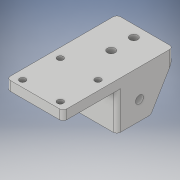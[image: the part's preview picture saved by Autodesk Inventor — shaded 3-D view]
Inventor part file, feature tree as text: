
AUTODESK INVENTOR PART (.ipt)
format: ipt  version: 2018 (Build 220112000, 112)  size: 181,248 bytes
history: native  units: in
note: dims shown in document units (in); Inventor stores cm internally (conversion verified against a paired STEP export)
features: extrude x6, sketch x6, mirror x1, fillet x1
ambient origin geometry x8: Origin, YZ Plane, XZ Plane, XY Plane, X Axis, Y Axis, Z Axis, Center Point
bodies: Solid1 (feature_tree)
feature tree (14):
  extrude  "Extrusion1"  Depth=2.3031in
  extrude  "Extrusion2"  Depth=0.1969in
  extrude  "Extrusion3"  Depth=0.7874in
  extrude  "Extrusion4"  Depth=0.1969in TaperAngle=0.0deg
  extrude  "Extrusion5"  Depth=0.9843in
  mirror  "Mirror1"
  extrude  "Extrusion6"  Depth=0.0787in
  fillet  "Fillet1"  Radius=0.4724in
  sketch  "Sketch1"  dims[d0=1.1811in d1=2.3031in]
  sketch  "Sketch2"  dims[d2=0.1969in d3=0.0in d4=0.126in]
  sketch  "Sketch3"  dims[d5=0.7874in d6=0.7874in]
  sketch  "Sketch4"  dims[d7=0.1378in d8=0.1969in d9=0.0in]
  sketch  "Sketch5"  dims[d10=0.7874in d11=0.9843in]
  sketch  "Sketch6"  dims[d12=0.1654in d13=0.2362in d14=0.4724in d15=0.1969in d16=0.0in d17=0.1969in d18=0.7874in d19=0.7087in d20=0.1969in d21=0.0in d25=0.1969in d26=0.0in d27=0.1969in d28=0.0in d29=0.1654in d30=0.0787in]
